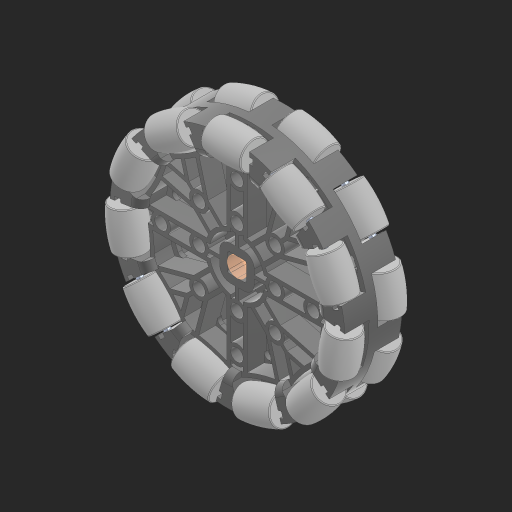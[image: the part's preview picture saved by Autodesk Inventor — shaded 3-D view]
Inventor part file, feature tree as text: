
AUTODESK INVENTOR PART (.ipt)
format: ipt  version: 2023 (Build 270158000, 158)  size: 3,479,040 bytes
history: native  units: in
note: dims shown in document units (in); Inventor stores cm internally (conversion verified against a paired STEP export)
features: other x47, move_body x1, sketch x1, extrude x1
ambient origin geometry x8: Origin, YZ Plane, XZ Plane, XY Plane, X Axis, Y Axis, Z Axis, Center Point
bodies: Solid1 (feature_tree), Solid2 (feature_tree), Solid3 (feature_tree), Solid4 (feature_tree), Solid5 (feature_tree), Solid6 (feature_tree), Solid7 (feature_tree), Solid8 (feature_tree), Solid9 (feature_tree), Solid10 (feature_tree), Solid11 (feature_tree), Solid12 (feature_tree), Solid13 (feature_tree), Solid14 (feature_tree), Solid15 (feature_tree), Solid16 (feature_tree), Solid17 (feature_tree), Solid18 (feature_tree), Solid19 (feature_tree), Solid20 (feature_tree), Solid21 (feature_tree), Solid22 (feature_tree), Solid23 (feature_tree), Solid24 (feature_tree), Solid25 (feature_tree), Solid26 (feature_tree), Solid27 (feature_tree), Solid28 (feature_tree), Solid29 (feature_tree), Solid30 (feature_tree), Solid31 (feature_tree), Solid32 (feature_tree), Solid33 (feature_tree), Solid34 (feature_tree), Solid35 (feature_tree), Solid36 (feature_tree), Solid37 (feature_tree), Solid38 (feature_tree), Solid39 (feature_tree), Solid40 (feature_tree), Solid41 (feature_tree), Solid42 (feature_tree), Solid43 (feature_tree), Solid44 (feature_tree), Solid45 (feature_tree)
feature tree (50):
  other  "3.25 (260mm Travel) Omni-Directional Anti-Static Wheel (276-8026).iam"
  other  "276-8026-001 Web.ipt:1"
  other  "276-8026-002 Web.iam:1::276-3526-001 Web.ipt:1"
  other  "276-8026-002 Web.iam:1::276-8026-003 Web.ipt:1"
  other  "276-8026-002 Web_1.iam:1::276-3526-001 Web.ipt:1"
  other  "276-8026-002 Web_1.iam:1::276-8026-003 Web.ipt:1"
  other  "276-8026-002 Web_2.iam:1::276-3526-001 Web.ipt:1"
  other  "276-8026-002 Web_2.iam:1::276-8026-003 Web.ipt:1"
  other  "276-8026-002 Web_3.iam:1::276-3526-001 Web.ipt:1"
  other  "276-8026-002 Web_3.iam:1::276-8026-003 Web.ipt:1"
  other  "276-8026-002 Web_4.iam:1::276-3526-001 Web.ipt:1"
  other  "276-8026-002 Web_4.iam:1::276-8026-003 Web.ipt:1"
  other  "276-8026-002 Web_5.iam:1::276-3526-001 Web.ipt:1"
  other  "276-8026-002 Web_5.iam:1::276-8026-003 Web.ipt:1"
  other  "276-8026-002 Web_6.iam:1::276-3526-001 Web.ipt:1"
  other  "276-8026-002 Web_6.iam:1::276-8026-003 Web.ipt:1"
  other  "276-8026-002 Web_7.iam:1::276-3526-001 Web.ipt:1"
  other  "276-8026-002 Web_7.iam:1::276-8026-003 Web.ipt:1"
  other  "276-8026-002 Web_8.iam:1::276-3526-001 Web.ipt:1"
  other  "276-8026-002 Web_8.iam:1::276-8026-003 Web.ipt:1"
  other  "276-8026-002 Web_9.iam:1::276-3526-001 Web.ipt:1"
  other  "276-8026-002 Web_9.iam:1::276-8026-003 Web.ipt:1"
  other  "276-8026-002 Web_10.iam:1::276-3526-001 Web.ipt:1"
  other  "276-8026-002 Web_10.iam:1::276-8026-003 Web.ipt:1"
  other  "276-8026-002 Web_11.iam:1::276-3526-001 Web.ipt:1"
  other  "276-8026-002 Web_11.iam:1::276-8026-003 Web.ipt:1"
  other  "276-8026-002 Web_12.iam:1::276-3526-001 Web.ipt:1"
  other  "276-8026-002 Web_12.iam:1::276-8026-003 Web.ipt:1"
  other  "276-8026-002 Web_13.iam:1::276-3526-001 Web.ipt:1"
  other  "276-8026-002 Web_13.iam:1::276-8026-003 Web.ipt:1"
  other  "276-8026-002 Web_14.iam:1::276-3526-001 Web.ipt:1"
  other  "276-8026-002 Web_14.iam:1::276-8026-003 Web.ipt:1"
  other  "276-8026-002 Web_15.iam:1::276-3526-001 Web.ipt:1"
  other  "276-8026-002 Web_15.iam:1::276-8026-003 Web.ipt:1"
  other  "276-8026-002 Web_16.iam:1::276-3526-001 Web.ipt:1"
  other  "276-8026-002 Web_16.iam:1::276-8026-003 Web.ipt:1"
  other  "276-8026-002 Web_17.iam:1::276-3526-001 Web.ipt:1"
  other  "276-8026-002 Web_17.iam:1::276-8026-003 Web.ipt:1"
  other  "276-8026-002 Web_18.iam:1::276-3526-001 Web.ipt:1"
  other  "276-8026-002 Web_18.iam:1::276-8026-003 Web.ipt:1"
  other  "276-8026-002 Web_19.iam:1::276-3526-001 Web.ipt:1"
  other  "276-8026-002 Web_19.iam:1::276-8026-003 Web.ipt:1"
  other  "276-8026-002 Web_20.iam:1::276-3526-001 Web.ipt:1"
  other  "276-8026-002 Web_20.iam:1::276-8026-003 Web.ipt:1"
  other  "276-8026-002 Web_21.iam:1::276-3526-001 Web.ipt:1"
  other  "276-8026-002 Web_21.iam:1::276-8026-003 Web.ipt:1"
  move_body  "Move Body1"
  sketch  "Sketch1"  dims[d0=0.3937in d1=90.0deg d2=0.25in d3=1.0in d4=0.0in]
  other  "Srf1"
  extrude  "ExtrusionSrf1"  TaperAngle=90.0deg  [1 undecoded]
note: 1 required parameter value undecoded (feature->parameter linkage not recoverable at this tier; creation-order binding heuristic only, values carry confidence <= 0.55)
